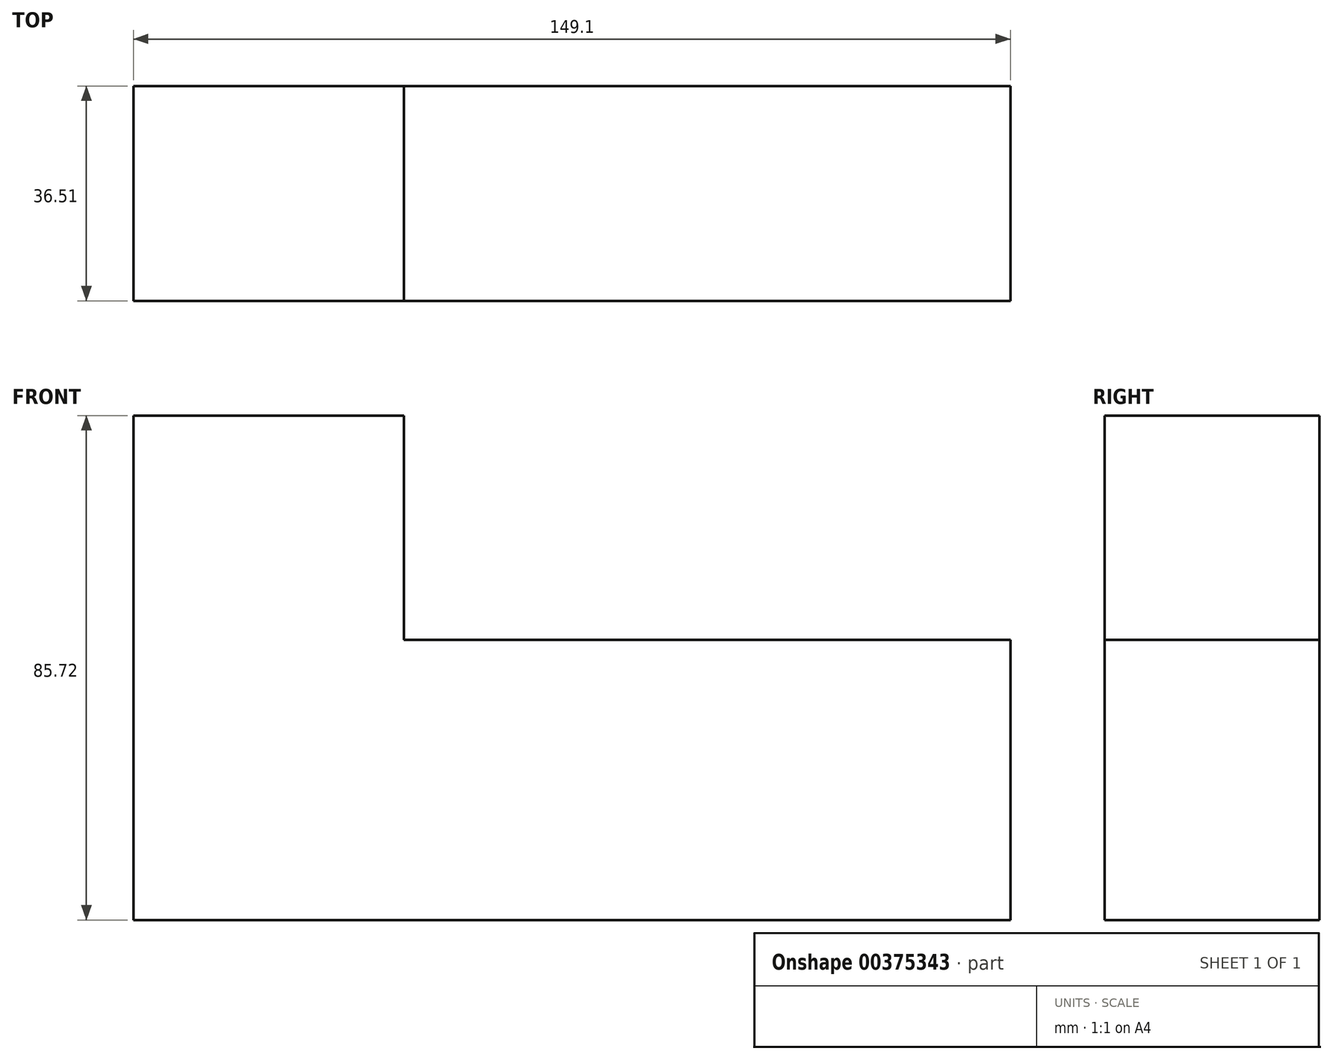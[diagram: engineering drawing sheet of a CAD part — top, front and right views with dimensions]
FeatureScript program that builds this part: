
annotation { "Feature Type Name" : "Feature", "Feature Type Description" : "" }
export const myFeature = defineFeature(function(context is Context, id is Id, definition is map)
    precondition{}
    {
        {
            var Q0;
            Q0=qCreatedBy(makeId("Front.planeOp"),FACE);
            var sketch = newSketch(context, id + "F0", { "sketchPlane" : qUnion([Q0])});
            skLineSegment(sketch, "E0", {"start": v(-81.84, 47.72) * mm, "end": v(-81.84, -38) * mm});
            skLineSegment(sketch, "E1", {"start": v(-81.84, -38) * mm, "end": v(67.26, -38) * mm});
            skLineSegment(sketch, "E2", {"start": v(-81.84, 47.72) * mm, "end": v(-35.86, 47.72) * mm});
            skLineSegment(sketch, "E3", {"start": v(-35.86, 47.72) * mm, "end": v(-35.86, 9.62) * mm});
            skLineSegment(sketch, "E4", {"start": v(-35.86, 9.62) * mm, "end": v(67.26, 9.62) * mm});
            skLineSegment(sketch, "E5", {"start": v(67.26, 9.62) * mm, "end": v(67.26, -38) * mm});
            skSolve(sketch);
        }
        {
            var Q0;
            Q0 = qSketchRegion(id + "F0", true);
            extrude(context, id + "F1", {"entities" : qUnion([Q0]), "depth" : 36.5 * mm});
        }
    });
